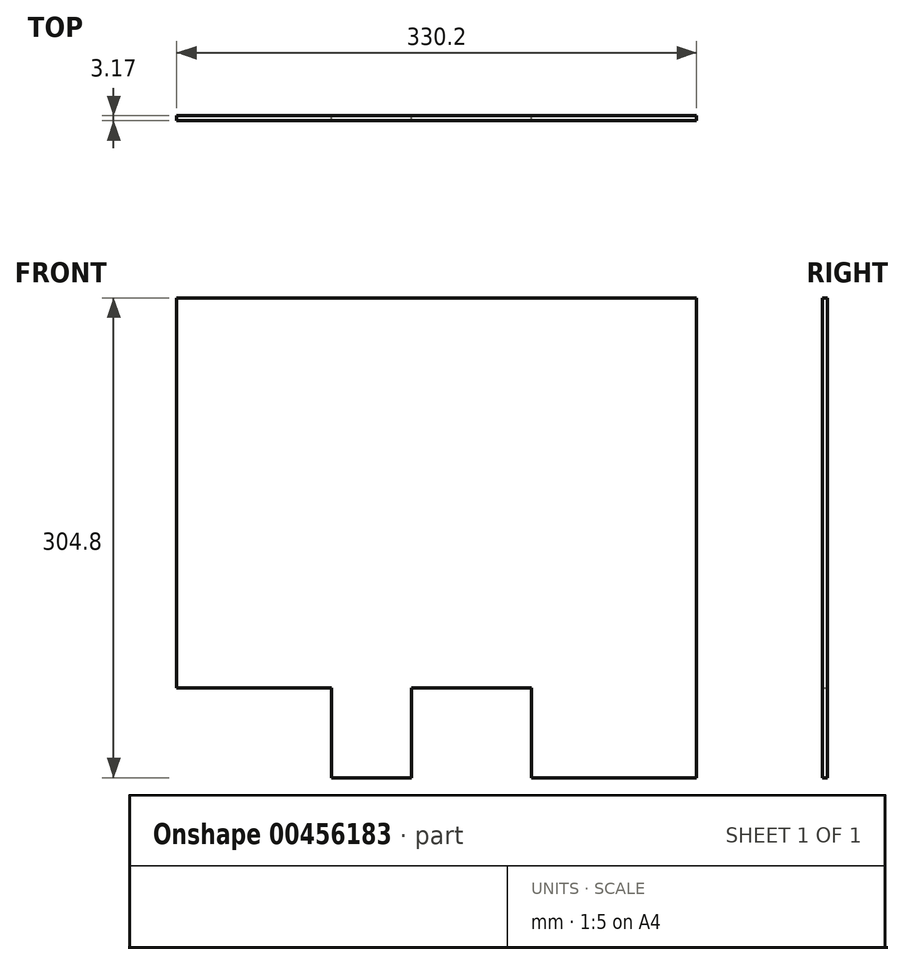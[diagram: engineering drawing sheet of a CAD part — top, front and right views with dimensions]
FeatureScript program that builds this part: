
annotation { "Feature Type Name" : "Feature", "Feature Type Description" : "" }
export const myFeature = defineFeature(function(context is Context, id is Id, definition is map)
    precondition{}
    {
        {
            var Q0;
            Q0=qCreatedBy(makeId("Front.planeOp"),FACE);
            var sketch = newSketch(context, id + "F0", { "sketchPlane" : qUnion([Q0])});
            skLineSegment(sketch, "E0.bottom", {"start": v(-46.9, -74.18) * mm, "end": v(3.9, -74.18) * mm});
            skLineSegment(sketch, "E0.top", {"start": v(-145.32, 230.62) * mm, "end": v(140.43, 230.62) * mm});
            skLineSegment(sketch, "E0.left", {"start": v(-145.32, -17.03) * mm, "end": v(-145.32, 230.62) * mm});
            skLineSegment(sketch, "E1", {"start": v(107.4, -74.18) * mm, "end": v(107.4, 119.5) * mm, "construction": true});
            skLineSegment(sketch, "E2", {"start": v(140.43, 119.5) * mm, "end": v(107.4, 119.5) * mm, "construction": true});
            skLineSegment(sketch, "E3.top", {"start": v(-145.32, -17.03) * mm, "end": v(-46.9, -17.03) * mm});
            skLineSegment(sketch, "E3.right", {"start": v(-46.9, -74.18) * mm, "end": v(-46.9, -17.03) * mm});
            skLineSegment(sketch, "E4.top", {"start": v(3.9, -17.03) * mm, "end": v(80.1, -17.03) * mm});
            skLineSegment(sketch, "E4.left", {"start": v(3.9, -74.18) * mm, "end": v(3.9, -17.03) * mm});
            skLineSegment(sketch, "E4.right", {"start": v(80.1, -74.18) * mm, "end": v(80.1, -17.03) * mm});
            skLineSegment(sketch, "E5.trimOffspring", {"start": v(80.1, -74.18) * mm, "end": v(107.4, -74.18) * mm});
            skPoint(sketch, "E6.end.orphan", {"position": v(3.9, 79.1) * mm});
            skLineSegment(sketch, "E7.bottom", {"start": v(140.43, 230.62) * mm, "end": v(184.88, 230.62) * mm});
            skLineSegment(sketch, "E7.left", {"start": v(140.43, 119.5) * mm, "end": v(140.43, -17.03) * mm, "construction": true});
            skLineSegment(sketch, "E7.right", {"start": v(184.88, 230.62) * mm, "end": v(184.88, -17.03) * mm});
            skLineSegment(sketch, "E8.top", {"start": v(140.43, -17.03) * mm, "end": v(184.88, -17.03) * mm});
            skPoint(sketch, "E9.orphan", {"position": v(184.88, -74.18) * mm});
            skPoint(sketch, "E10.orphan", {"position": v(184.88, 171.37) * mm});
            skLineSegment(sketch, "E11.bottom", {"start": v(107.4, -74.18) * mm, "end": v(184.88, -74.18) * mm});
            skLineSegment(sketch, "E11.top", {"start": v(107.4, -17.03) * mm, "end": v(184.88, -17.03) * mm, "construction": true});
            skLineSegment(sketch, "E11.left", {"start": v(107.4, -74.18) * mm, "end": v(107.4, -17.03) * mm});
            skLineSegment(sketch, "E11.right", {"start": v(184.88, -74.18) * mm, "end": v(184.88, -17.03) * mm});
            skSolve(sketch);
        }
        {
            var Q0;
            Q0=makeQuery(id+"F0.imprint","IMPRINT",FACE,{"disambiguationData":[TD([[makeQuery(id+"F0.imprint","IMPRINT",EDGE,{"derivedFrom":sQuery(id+"F0.wireOp",EDGE,"E0.bottom")}),1.0]])]});
            extrude(context, id + "F1", {"entities" : qUnion([Q0]), "depth" : 3.17 * mm});
        }
    });
